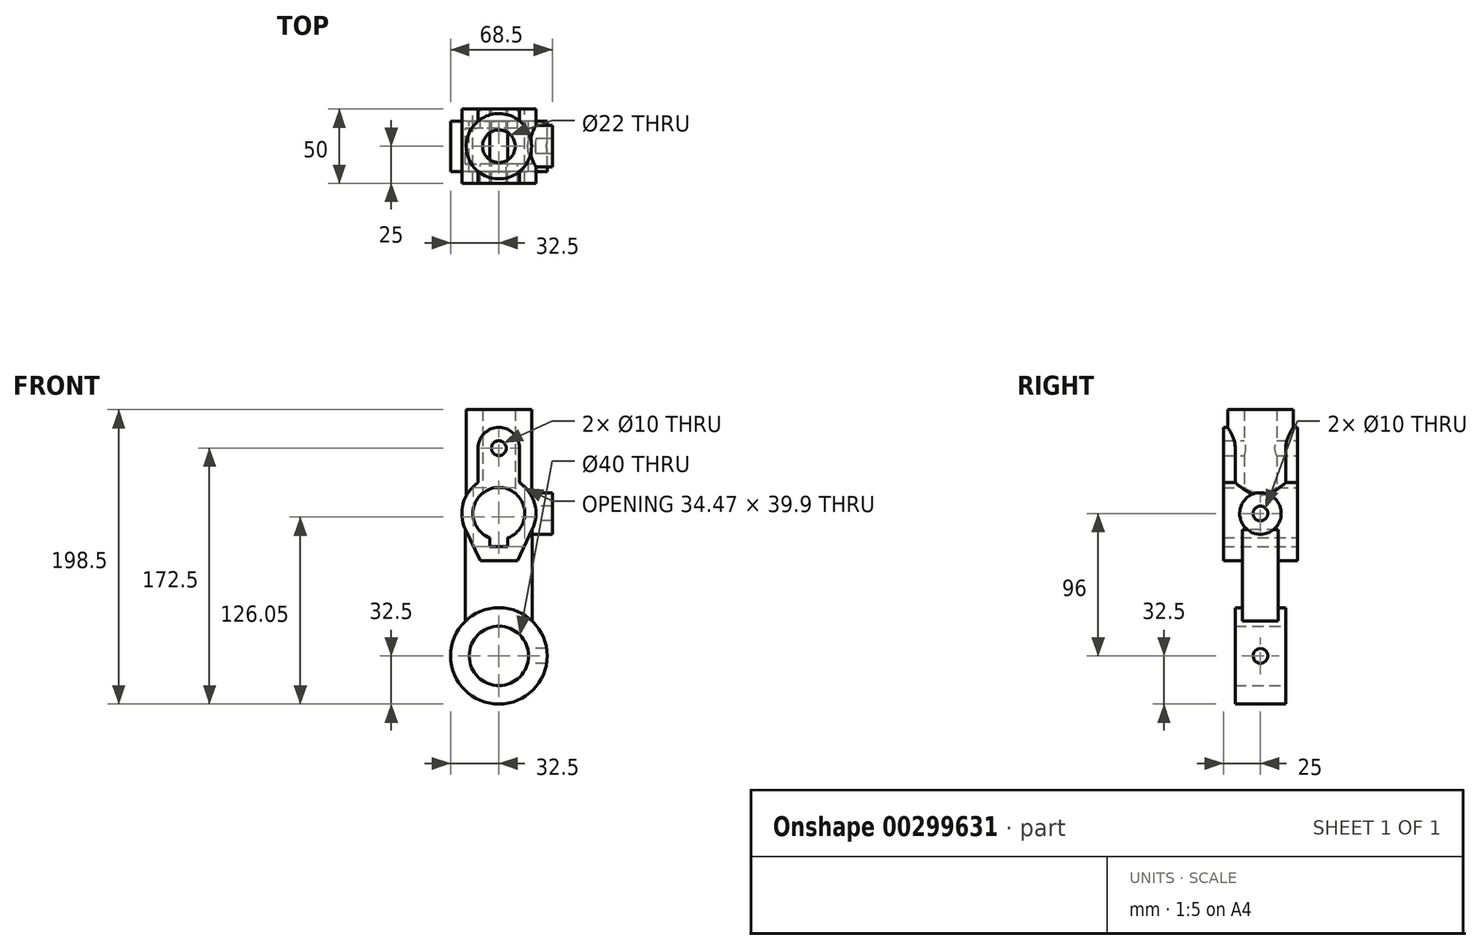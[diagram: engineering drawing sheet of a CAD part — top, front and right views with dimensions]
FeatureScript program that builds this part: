
annotation { "Feature Type Name" : "Feature", "Feature Type Description" : "" }
export const myFeature = defineFeature(function(context is Context, id is Id, definition is map)
    precondition{}
    {
        {
            var Q0;
            Q0=qCreatedBy(makeId("Front.planeOp"),FACE);
            var sketch = newSketch(context, id + "F0", { "sketchPlane" : qUnion([Q0])});
            skCircle(sketch, "E0", {"center": v(0, 0) * mm, "radius": 20 * mm});
            skCircle(sketch, "E1", {"center": v(0, 0) * mm, "radius": 32.5 * mm});
            skLineSegment(sketch, "E2", {"start": v(-22.5, 23.45) * mm, "end": v(-22.5, 96) * mm});
            skLineSegment(sketch, "E3", {"start": v(22.5, 96) * mm, "end": v(22.5, 23.45) * mm});
            skLineSegment(sketch, "E4", {"start": v(22.5, 96) * mm, "end": v(-22.5, 96) * mm});
            skLineSegment(sketch, "E5", {"start": v(0, 0) * mm, "end": v(0, 117.31) * mm, "construction": true});
            skLineSegment(sketch, "E6", {"start": v(0, 0) * mm, "end": v(47.11, 0) * mm, "construction": true});
            skLineSegment(sketch, "E7", {"start": v(0, 0) * mm, "end": v(-48.98, 0) * mm, "construction": true});
            skLineSegment(sketch, "E8", {"start": v(0, 0) * mm, "end": v(0, -45.08) * mm, "construction": true});
            skSolve(sketch);
        }
        {
            var Q0;
            {var subQ0=sQuery(id+"F0.wireOp",EDGE,"E2");Q0=makeQuery(id+"F0.imprint","IMPRINT",FACE,{"disambiguationData":[TD([[makeQuery(id+"F0.imprint","IMPRINT",EDGE,{"derivedFrom":subQ0}),-1.0]])]});}
            extrude(context, id + "F1", {"entities" : qUnion([Q0]), "depth" : 24 * mm, "symmetric" : true});
        }
        {
            var Q0;
            Q0=makeQuery(id+"F0.imprint","IMPRINT",FACE,{"disambiguationData":[TD([[makeQuery(id+"F0.imprint","IMPRINT",EDGE,{"derivedFrom":sQuery(id+"F0.wireOp",EDGE,"E0")}),-1.0]])]});
            extrude(context, id + "F2", {"entities" : qUnion([Q0]), "operationType" : NewBodyOperationType.ADD, "depth" : 34 * mm, "symmetric" : true});
        }
        {
            var Q0;
            Q0=qCreatedBy(makeId("Front.planeOp"),FACE);
            var sketch = newSketch(context, id + "F3", { "sketchPlane" : qUnion([Q0])});
            skArc(sketch, "E9", {"start": v(6, 79.56) * mm, "mid": v(0, 113.5) * mm, "end": v(-6, 79.56) * mm});
            skLineSegment(sketch, "E10", {"start": v(6, 79.56) * mm, "end": v(6, 73.6) * mm});
            skLineSegment(sketch, "E11", {"start": v(6, 73.6) * mm, "end": v(-6, 73.6) * mm});
            skLineSegment(sketch, "E12", {"start": v(-6, 73.6) * mm, "end": v(-6, 79.56) * mm});
            skCircle(sketch, "E13", {"center": v(0, 140) * mm, "radius": 5 * mm});
            skLineSegment(sketch, "E14", {"start": v(0, 96) * mm, "end": v(0, 151.57) * mm, "construction": true});
            skLineSegment(sketch, "E15", {"start": v(0, 96) * mm, "end": v(46.1, 96) * mm, "construction": true});
            skLineSegment(sketch, "E16", {"start": v(0, 96) * mm, "end": v(-36.15, 96) * mm, "construction": true});
            skArc(sketch, "E17", {"start": v(14, 140) * mm, "mid": v(0, 154) * mm, "end": v(-14, 140) * mm});
            skLineSegment(sketch, "E18", {"start": v(14, 140) * mm, "end": v(14, 116.71) * mm});
            skLineSegment(sketch, "E19", {"start": v(-14, 140) * mm, "end": v(-14, 116.71) * mm});
            skLineSegment(sketch, "E20", {"start": v(-12.5, 64) * mm, "end": v(12.5, 64) * mm});
            skLineSegment(sketch, "E21", {"start": v(12.5, 64) * mm, "end": v(22.6, 85.3) * mm});
            skLineSegment(sketch, "E22", {"start": v(-12.5, 64) * mm, "end": v(-22.6, 85.3) * mm});
            skArc(sketch, "E23", {"start": v(-22.6, 85.3) * mm, "mid": v(-24.11, 102.6) * mm, "end": v(-14, 116.71) * mm});
            skArc(sketch, "E24", {"start": v(22.6, 85.3) * mm, "mid": v(24.11, 102.6) * mm, "end": v(14, 116.71) * mm});
            skSolve(sketch);
        }
        {
            var Q0;
            Q0=makeQuery(id+"F3.imprint","IMPRINT",FACE,{"disambiguationData":[TD([[makeQuery(id+"F3.imprint","IMPRINT",EDGE,{"derivedFrom":sQuery(id+"F3.wireOp",EDGE,"E9")}),-1.0]])]});
            extrude(context, id + "F4", {"entities" : qUnion([Q0]), "operationType" : NewBodyOperationType.ADD, "depth" : 50 * mm, "symmetric" : true});
        }
        {
            var Q0;
            {var subQ0=sQuery(id+"F0.wireOp",EDGE,"E4");Q0=makeQuery(id+"F4.boolean.opBoolean","SPLIT",FACE,{"disambiguationData":[TD([makeQuery(id+"F1.opExtrude","SWEPT_FACE",FACE,{"disambiguationData":[OSD([subQ0])]})])],"derivedFrom":makeQuery(id+"F1.opExtrude","CAP_FACE",FACE,{"disambiguationData":[OSD([sQuery(id+"F0.wireOp",EDGE,"E1"),sQuery(id+"F0.wireOp",EDGE,"E2"),sQuery(id+"F0.wireOp",EDGE,"E3"),subQ0])],"isStart":false})});}
            extrude(context, id + "F5", {"entities" : qUnion([Q0]), "operationType" : NewBodyOperationType.REMOVE, "endBound" : BoundingType.THROUGH_ALL, "oppositeDirection" : true, "depth" : 25 * mm});
        }
        {
            var Q0;
            Q0=qCreatedBy(makeId("Right.planeOp"),FACE);
            var sketch = newSketch(context, id + "F6", { "sketchPlane" : qUnion([Q0])});
            skPoint(sketch, "E25.0", {"position": v(0, 96) * mm});
            skCircle(sketch, "E26", {"center": v(0, 96) * mm, "radius": 5 * mm});
            skCircle(sketch, "E27", {"center": v(0, 96) * mm, "radius": 14 * mm});
            skSolve(sketch);
        }
        {
            var Q0;
            Q0=makeQuery(id+"F6.imprint","IMPRINT",FACE,{"disambiguationData":[TD([[makeQuery(id+"F6.imprint","IMPRINT",EDGE,{"derivedFrom":sQuery(id+"F6.wireOp",EDGE,"E26")}),-1.0]])]});
            extrude(context, id + "F7", {"entities" : qUnion([Q0]), "operationType" : NewBodyOperationType.ADD, "depth" : 36 * mm});
        }
        {
            var Q0;
            Q0=qCreatedBy(makeId("Front.planeOp"),FACE);
            var sketch = newSketch(context, id + "F8", { "sketchPlane" : qUnion([Q0])});
            skPoint(sketch, "E28.0", {"position": v(0, 96) * mm});
            skCircle(sketch, "E29", {"center": v(0, 96) * mm, "radius": 17.5 * mm});
            skSolve(sketch);
        }
        {
            var Q0;
            Q0=makeQuery(id+"F8.imprint","IMPRINT",FACE,{"disambiguationData":[TD([[makeQuery(id+"F8.imprint","IMPRINT",EDGE,{"derivedFrom":sQuery(id+"F8.wireOp",EDGE,"E29")}),1.0]])]});
            extrude(context, id + "F9", {"entities" : qUnion([Q0]), "operationType" : NewBodyOperationType.REMOVE, "endBound" : BoundingType.THROUGH_ALL, "oppositeDirection" : true, "depth" : 25 * mm, "hasSecondDirection" : true, "secondDirectionBound" : BoundingType.THROUGH_ALL, "secondDirectionOppositeDirection" : false, "secondDirectionDepth" : 25 * mm});
        }
        {
            var Q0;
            Q0=qCreatedBy(makeId("Right.planeOp"),FACE);
            var sketch = newSketch(context, id + "F10", { "sketchPlane" : qUnion([Q0])});
            skCircle(sketch, "E30", {"center": v(0, 0) * mm, "radius": 5 * mm});
            skSolve(sketch);
        }
        {
            var Q0;
            Q0 = qSketchRegion(id + "F10", true);
            extrude(context, id + "F11", {"entities" : qUnion([Q0]), "operationType" : NewBodyOperationType.REMOVE, "endBound" : BoundingType.THROUGH_ALL, "depth" : 25 * mm});
        }
        {
            var Q0;
            Q0=sQuery(id+"F0.wireOp",EDGE,"E4");
            cPoint(context, id + "F12", {"entities" : qUnion([Q0]), "parameter" : 0.5});
        }
        {
            var Q0;
            Q0=qCreatedBy(makeId("Top.planeOp"),FACE);
            var Q1;
            Q1 = qCreatedBy(id + "F12" ,VERTEX);
            cPlane(context, id + "F13", {"entities" : qUnion([Q0, Q1]), "cplaneType" : CPlaneType.PLANE_POINT, "offset" : 25 * mm, "width" : 150 * mm, "height" : 150 * mm});
        }
        {
            var Q0;
            Q0=qCreatedBy(id+"F13.planeOp",FACE);
            var sketch = newSketch(context, id + "F14", { "sketchPlane" : qUnion([Q0])});
            skCircle(sketch, "E31", {"center": v(0, 0) * mm, "radius": 11 * mm});
            skCircle(sketch, "E32", {"center": v(0, 0) * mm, "radius": 22 * mm});
            skSolve(sketch);
        }
        {
            var Q0;
            Q0=makeQuery(id+"F14.imprint","IMPRINT",FACE,{"disambiguationData":[TD([[makeQuery(id+"F14.imprint","IMPRINT",EDGE,{"derivedFrom":sQuery(id+"F14.wireOp",EDGE,"E31")}),1.0]])]});
            extrude(context, id + "F15", {"entities" : qUnion([Q0]), "operationType" : NewBodyOperationType.REMOVE, "endBound" : BoundingType.THROUGH_ALL, "depth" : 25 * mm});
        }
        {
            var Q0;
            Q0=makeQuery(id+"F14.imprint","IMPRINT",FACE,{"disambiguationData":[TD([[makeQuery(id+"F14.imprint","IMPRINT",EDGE,{"derivedFrom":sQuery(id+"F14.wireOp",EDGE,"E31")}),-1.0]])]});
            extrude(context, id + "F16", {"entities" : qUnion([Q0]), "operationType" : NewBodyOperationType.ADD, "depth" : 70 * mm});
        }
        {
            var Q0;
            Q0 = qSketchRegion(id + "F8", true);
            extrude(context, id + "F17", {"entities" : qUnion([Q0]), "operationType" : NewBodyOperationType.REMOVE, "endBound" : BoundingType.THROUGH_ALL, "oppositeDirection" : true, "depth" : 25 * mm, "hasSecondDirection" : true, "secondDirectionBound" : BoundingType.THROUGH_ALL, "secondDirectionOppositeDirection" : false, "secondDirectionDepth" : 25 * mm});
        }
        {
            var Q0;
            Q0=makeQuery(id+"F4.opExtrude","CAP_FACE",FACE,{"disambiguationData":[OSD([sQuery(id+"F3.wireOp",EDGE,"E9"),sQuery(id+"F3.wireOp",EDGE,"E10"),sQuery(id+"F3.wireOp",EDGE,"E11"),sQuery(id+"F3.wireOp",EDGE,"E12"),sQuery(id+"F3.wireOp",EDGE,"E13"),sQuery(id+"F3.wireOp",EDGE,"E17"),sQuery(id+"F3.wireOp",EDGE,"E18"),sQuery(id+"F3.wireOp",EDGE,"E19"),sQuery(id+"F3.wireOp",EDGE,"E20"),sQuery(id+"F3.wireOp",EDGE,"E21"),sQuery(id+"F3.wireOp",EDGE,"E22"),sQuery(id+"F3.wireOp",EDGE,"E23"),sQuery(id+"F3.wireOp",EDGE,"E24")])],"isStart":false});
            var sketch = newSketch(context, id + "F18", { "sketchPlane" : qUnion([Q0])});
            skCircle(sketch, "E33", {"center": v(0, 140) * mm, "radius": 5 * mm});
            skSolve(sketch);
        }
        {
            var Q0;
            Q0=makeQuery(id+"F18.imprint","IMPRINT",FACE,{"disambiguationData":[TD([[makeQuery(id+"F18.imprint","IMPRINT",EDGE,{"derivedFrom":sQuery(id+"F18.wireOp",EDGE,"E33")}),1.0]])]});
            extrude(context, id + "F19", {"entities" : qUnion([Q0]), "operationType" : NewBodyOperationType.REMOVE, "endBound" : BoundingType.THROUGH_ALL, "oppositeDirection" : true, "depth" : 25 * mm});
        }
    });
